# Revit family: Bottle_Filling_Station-Murdock-BF1S
name_source: partatom
category: Plumbing Fixtures
units: mm (PartAtom-declared; Revit-internal decimal feet)

## family parameters
Cut with Voids When Loaded = No
Host = Face
OmniClass Number = 23.65.70.14.11
OmniClass Title = Drinking Fountains/Coolers
Part Type = Normal
Room Calculation Point = No
Round Connector Dimension = Use Diameter
Shared = Yes

## types (1)
- BF1S
    -WF1 1500-gallon capacity, NSF 42+53, 1 micron Lead Reduction Water Filter = No
    ADA Compliant = Yes
    Activation = Push Button
    Assembly Code = D2010820
    CW Connection = Yes
    CWFU = 1.5
    Compliance Certifications = ANSI A117.1, Public Law 111-380 (NO-LEAD), CHSC 116875 and NSF/ANSI 61, Section 9.
    Default Elevation = 0"
    Description = Deck-Mounted, Heavy-Duty, Push Button Water Bottle Filling Station (A17 Series Add-On) - Stainless Steel
    Fill Rate = 1 GPM
    Finish = Metal-Murdock-Stainless Steel
    HW Connection = No
    HWFU = 1.5
    Height = 16"
    Inlet Connection Diameter = 1/2"
    Installation Type = Wall/Deck Mounted
    Length = 16 1/2"
    Manufacturer = Murdock
    Material = Metal-Murdock-Stainless Steel
    Model = BF1S
    Product Documentation Link = https://www.murdockmfg.com
    Product Page URL = https://www.murdockmfg.com
    Revised Date = 09/27/2022
    URL = https://www.murdockmfg.com
    Vent Connection = No
    WFU = 2
    Warranty Information = Murdock Mfg.™ warrants that its products are free from defects in material or workmanship under normal use and service for a period of one year from date of shipment.
    Waste Connection = No
    Width = 4"
    cUPC Compliant = Yes

## geometry (parser evidence)
native form markers: Sweep x3
no freeform markers — native parametric forms only
